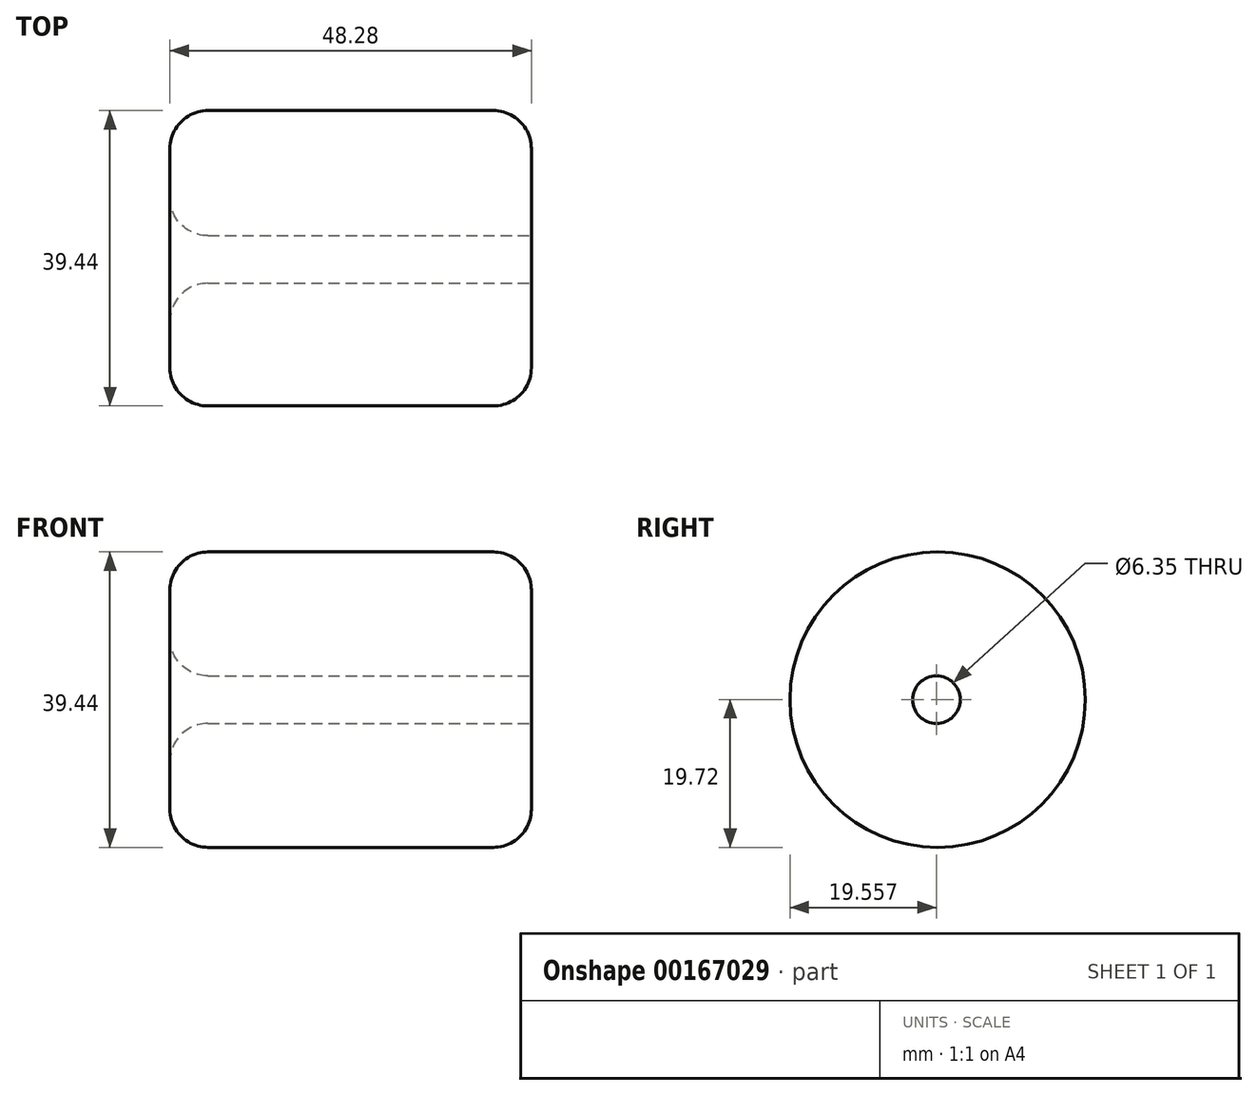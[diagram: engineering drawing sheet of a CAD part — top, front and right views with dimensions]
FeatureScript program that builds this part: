
annotation { "Feature Type Name" : "Feature", "Feature Type Description" : "" }
export const myFeature = defineFeature(function(context is Context, id is Id, definition is map)
    precondition{}
    {
        {
            var Q0;
            Q0=qCreatedBy(makeId("Top.planeOp"),FACE);
            var sketch = newSketch(context, id + "F0", { "sketchPlane" : qUnion([Q0])});
            skLineSegment(sketch, "E0.bottom", {"start": v(-57.42, -13.17) * mm, "end": v(-9.14, -13.17) * mm});
            skLineSegment(sketch, "E0.top", {"start": v(-57.42, 6.55) * mm, "end": v(-9.14, 6.55) * mm});
            skLineSegment(sketch, "E0.left", {"start": v(-57.42, -13.17) * mm, "end": v(-57.42, 6.55) * mm});
            skLineSegment(sketch, "E0.right", {"start": v(-9.14, -13.17) * mm, "end": v(-9.14, 6.55) * mm});
            skSolve(sketch);
        }
        {
            var Q0;
            Q0 = qSketchRegion(id + "F0", true);
            var Q1;
            Q1=makeQuery(id+"F0.imprint","IMPRINT",FACE,{"disambiguationData":[TD([[makeQuery(id+"F0.imprint","IMPRINT",EDGE,{"derivedFrom":sQuery(id+"F0.wireOp",EDGE,"E0.bottom")}),1.0]])]});
            var Q2;
            Q2=sQuery(id+"F0.wireOp",EDGE,"E0.top");
            revolve(context, id + "F1", {"entities" : qUnion([Q0, Q1]), "axis" : qUnion([Q2]), "revolveType" : RevolveType.FULL});
        }
        {
            var Q0;
            Q0=qCreatedBy(makeId("Right.planeOp"),FACE);
            var sketch = newSketch(context, id + "F2", { "sketchPlane" : qUnion([Q0])});
            skCircle(sketch, "E1", {"center": v(6.39, 0) * mm, "radius": 9.27 * mm});
            skSolve(sketch);
        }
        {
            var Q0;
            Q0=sQuery(id+"F2.wireOp",VERTEX,"E1.center");
            var Q1;
            Q1=makeQuery(id+"F1.opRevolve","SWEPT_BODY",BODY,{"disambiguationData":[OSD([sQuery(id+"F0.wireOp",EDGE,"E0.bottom"),sQuery(id+"F0.wireOp",EDGE,"E0.top"),sQuery(id+"F0.wireOp",EDGE,"E0.left"),sQuery(id+"F0.wireOp",EDGE,"E0.right")])]});
            hole(context, id + "F3", {"style" : HoleStyle.SIMPLE, "endStyle" : HoleEndStyle.THROUGH, "holeDiameter" : 6.35 * mm, "locations" : qUnion([Q0]), "scope" : qUnion([Q1]), "isTappedThrough" : true});
        }
        {
            var Q0;
            Q0=makeQuery(id+"F1.opRevolve","SWEPT_FACE",FACE,{"disambiguationData":[OSD([sQuery(id+"F0.wireOp",EDGE,"E0.left")])]});
            var Q1;
            Q1=makeQuery(id+"F1.opRevolve","SWEPT_FACE",FACE,{"disambiguationData":[OSD([sQuery(id+"F0.wireOp",EDGE,"E0.bottom")])]});
            var Q2;
            Q2=makeQuery(id+"F1.opRevolve","SWEPT_EDGE",EDGE,{"disambiguationData":[OSD([sQuery(id+"F0.wireOp",EDGE,"E0.bottom"),sQuery(id+"F0.wireOp",EDGE,"E0.right")])]});
            var Q3;
            Q3=makeQuery(id+"F1.opRevolve","SWEPT_EDGE",EDGE,{"disambiguationData":[OSD([sQuery(id+"F0.wireOp",EDGE,"E0.bottom"),sQuery(id+"F0.wireOp",EDGE,"E0.left")])]});
            var Q4;
            Q4=makeQuery(id+"F3.hole-0.boolean.opBoolean","INTERSECT",EDGE,{"derivedFrom":[makeQuery(id+"F1.opRevolve","SWEPT_FACE",FACE,{"disambiguationData":[OSD([sQuery(id+"F0.wireOp",EDGE,"E0.right")])]}),makeQuery(id+"F3.hole-0.opRevolve","SWEPT_FACE",FACE,{"disambiguationData":[OSD([sQuery(id+"F3.hole-0.sketch.wireOp",EDGE,"core_line_2")])]})]});
            fillet(context, id + "F4", {"entities" : qUnion([Q0, Q1, Q2, Q3, Q4]), "radius" : 5.08 * mm, "tangentPropagation" : true, "allowEdgeOverflow" : false});
        }
    });
